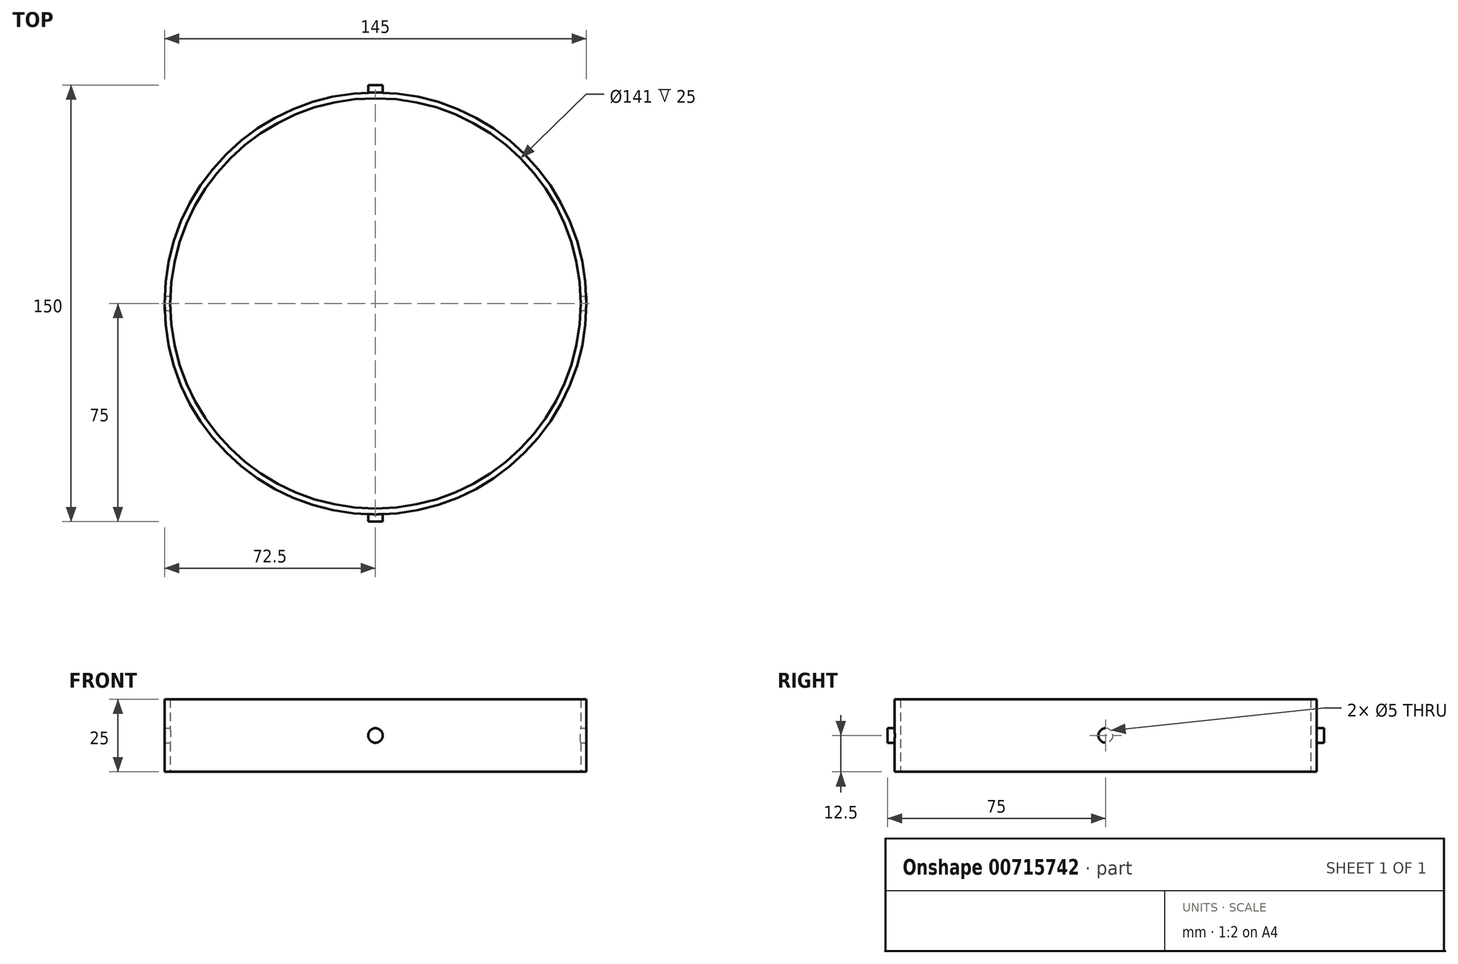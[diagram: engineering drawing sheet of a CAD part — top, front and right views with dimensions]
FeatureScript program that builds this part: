
annotation { "Feature Type Name" : "Feature", "Feature Type Description" : "" }
export const myFeature = defineFeature(function(context is Context, id is Id, definition is map)
    precondition{}
    {
        {
            var Q0;
            Q0=qCreatedBy(makeId("Top.planeOp"),FACE);
            var sketch = newSketch(context, id + "F0", { "sketchPlane" : qUnion([Q0])});
            skCircle(sketch, "E0", {"center": v(0, 0) * mm, "radius": 72.5 * mm});
            skCircle(sketch, "E1", {"center": v(0, 0) * mm, "radius": 70.5 * mm});
            skSolve(sketch);
        }
        {
            var Q0;
            Q0 = qSketchRegion(id + "F0", true);
            extrude(context, id + "F1", {"entities" : qUnion([Q0]), "depth" : 25 * mm, "offsetDistance" : 25 * mm, "symmetric" : true});
        }
        {
            var Q0;
            Q0=qCreatedBy(makeId("Front.planeOp"),FACE);
            var sketch = newSketch(context, id + "F2", { "sketchPlane" : qUnion([Q0])});
            skCircle(sketch, "E2", {"center": v(0, 0) * mm, "radius": 2.5 * mm});
            skSolve(sketch);
        }
        {
            var Q0;
            Q0 = qSketchRegion(id + "F2", true);
            extrude(context, id + "F3", {"entities" : qUnion([Q0]), "operationType" : NewBodyOperationType.ADD, "depth" : 150 * mm, "offsetDistance" : 25 * mm, "symmetric" : true});
        }
        {
            var Q0;
            Q0 = qSketchRegion(id + "F2", true);
            var Q1;
            Q1=makeQuery(id+"F1.opExtrude","SWEPT_FACE",FACE,{"disambiguationData":[OSD([sQuery(id+"F0.wireOp",EDGE,"E1")])]});
            var Q2;
            Q2=makeQuery(id+"F1.opExtrude","SWEPT_FACE",FACE,{"disambiguationData":[OSD([sQuery(id+"F0.wireOp",EDGE,"E1")])]});
            extrude(context, id + "F4", {"entities" : qUnion([Q0]), "operationType" : NewBodyOperationType.REMOVE, "endBound" : BoundingType.UP_TO_SURFACE, "oppositeDirection" : true, "depth" : 25 * mm, "endBoundEntityFace" : qUnion([Q1]), "offsetDistance" : 25 * mm, "hasSecondDirection" : true, "secondDirectionBound" : BoundingType.UP_TO_SURFACE, "secondDirectionOppositeDirection" : false, "secondDirectionDepth" : 25 * mm, "secondDirectionBoundEntityFace" : qUnion([Q2])});
        }
        {
            var Q0;
            Q0=qCreatedBy(makeId("Right.planeOp"),FACE);
            var sketch = newSketch(context, id + "F5", { "sketchPlane" : qUnion([Q0])});
            skCircle(sketch, "E3", {"center": v(0, 0) * mm, "radius": 2.5 * mm});
            skSolve(sketch);
        }
        {
            var Q0;
            Q0 = qSketchRegion(id + "F5", true);
            extrude(context, id + "F6", {"entities" : qUnion([Q0]), "operationType" : NewBodyOperationType.REMOVE, "endBound" : BoundingType.THROUGH_ALL, "oppositeDirection" : true, "depth" : 25 * mm, "offsetDistance" : 25 * mm, "hasSecondDirection" : true, "secondDirectionBound" : BoundingType.THROUGH_ALL, "secondDirectionOppositeDirection" : false, "secondDirectionDepth" : 25 * mm});
        }
    });
